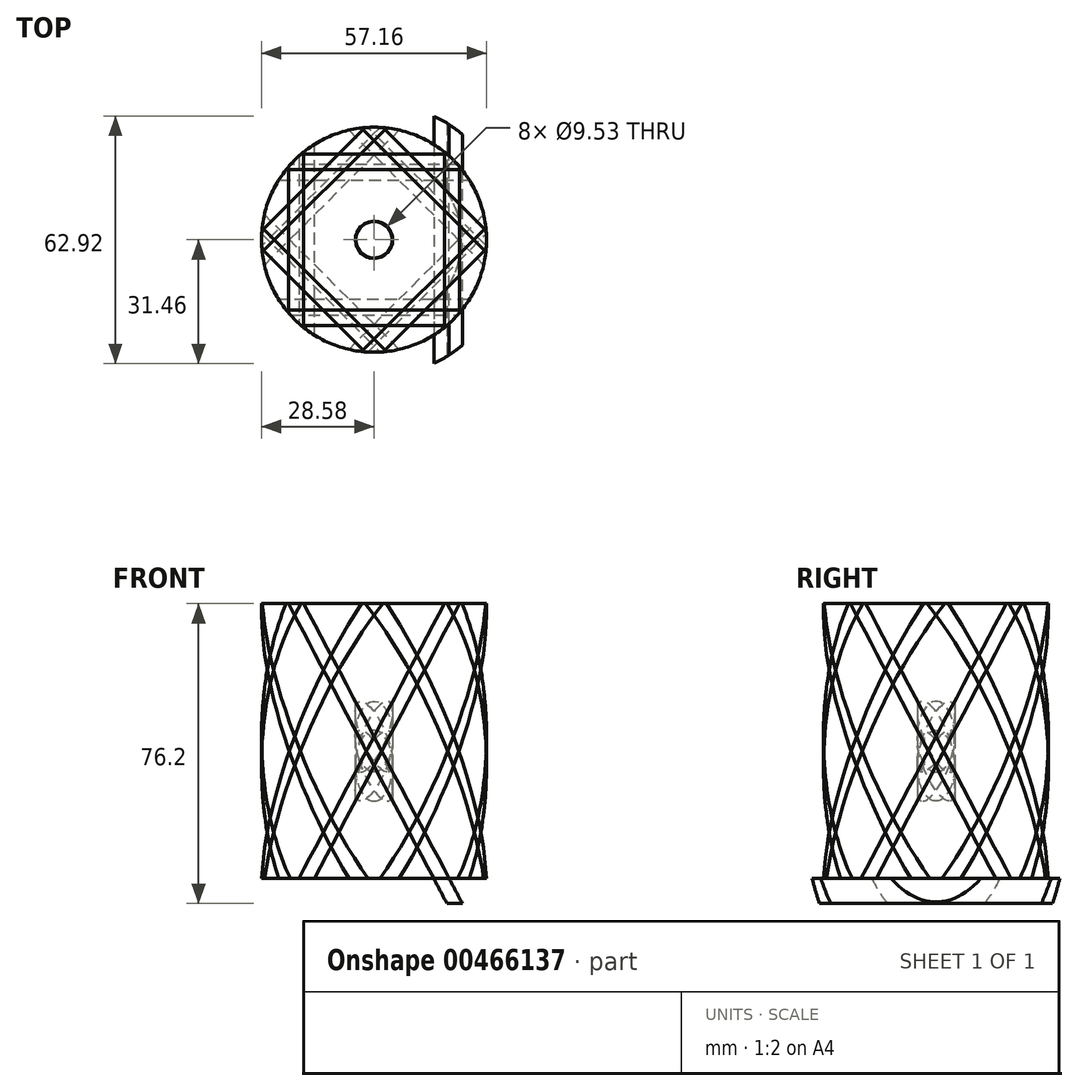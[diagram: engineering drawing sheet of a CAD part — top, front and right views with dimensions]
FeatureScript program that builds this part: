
annotation { "Feature Type Name" : "Feature", "Feature Type Description" : "" }
export const myFeature = defineFeature(function(context is Context, id is Id, definition is map)
    precondition{}
    {
        {
            var Q0;
            Q0=qCreatedBy(makeId("Top.planeOp"),FACE);
            var sketch = newSketch(context, id + "F0", { "sketchPlane" : qUnion([Q0])});
            skCircle(sketch, "E0", {"center": v(0, 0) * mm, "radius": 28.58 * mm});
            skCircle(sketch, "E1.0", {"center": v(0, 0) * mm, "radius": 22.22 * mm});
            skCircle(sketch, "E2", {"center": v(0, 0) * mm, "radius": 4.76 * mm});
            skCircle(sketch, "E3", {"center": v(0, 0) * mm, "radius": 34.93 * mm});
            skSolve(sketch);
        }
        {
            var Q0;
            Q0=qCreatedBy(makeId("Front.planeOp"),FACE);
            var sketch = newSketch(context, id + "F1", { "sketchPlane" : qUnion([Q0])});
            skLineSegment(sketch, "E4", {"start": v(-20.19, 74.24) * mm, "end": v(22.62, -6.7) * mm});
            skLineSegment(sketch, "E5", {"start": v(22.62, -6.7) * mm, "end": v(18.72, -6.7) * mm});
            skLineSegment(sketch, "E6", {"start": v(18.72, -6.7) * mm, "end": v(-24.1, 74.24) * mm});
            skLineSegment(sketch, "E7", {"start": v(-24.1, 74.24) * mm, "end": v(-20.19, 74.24) * mm});
            skLineSegment(sketch, "E8", {"start": v(0, 0) * mm, "end": v(0, 75.23) * mm, "construction": true});
            skSolve(sketch);
        }
        {
            var Q0;
            Q0=makeQuery(id+"F0.imprint","IMPRINT",FACE,{"disambiguationData":[TD([[makeQuery(id+"F0.imprint","IMPRINT",EDGE,{"derivedFrom":sQuery(id+"F0.wireOp",EDGE,"E0")}),-1.0]])]});
            var Q1;
            Q1=makeQuery(id+"F0.imprint","IMPRINT",FACE,{"disambiguationData":[TD([[makeQuery(id+"F0.imprint","IMPRINT",EDGE,{"derivedFrom":sQuery(id+"F0.wireOp",EDGE,"E0")}),1.0]])]});
            extrude(context, id + "F2", {"entities" : qUnion([Q0, Q1]), "oppositeDirection" : true, "depth" : 6.35 * mm});
        }
        {
            var Q0;
            Q0=makeQuery(id+"F0.imprint","IMPRINT",FACE,{"disambiguationData":[TD([[makeQuery(id+"F0.imprint","IMPRINT",EDGE,{"derivedFrom":sQuery(id+"F0.wireOp",EDGE,"E1.0")}),1.0]])]});
            var Q1;
            Q1=makeQuery(id+"F0.imprint","IMPRINT",FACE,{"disambiguationData":[TD([[makeQuery(id+"F0.imprint","IMPRINT",EDGE,{"derivedFrom":sQuery(id+"F0.wireOp",EDGE,"E0")}),1.0]])]});
            extrude(context, id + "F3", {"entities" : qUnion([Q0, Q1]), "depth" : 69.85 * mm});
        }
        {
            var Q0;
            Q0=qSketchRegion(id+"F1",true);
            extrude(context, id + "F4", {"entities" : qUnion([Q0]), "operationType" : NewBodyOperationType.INTERSECT, "depth" : 101.6 * mm, "symmetric" : true});
        }
        {
            var Q0;
            Q0=makeQuery(id+"F3.opExtrude","SWEPT_BODY",BODY,{"disambiguationData":[OSD([sQuery(id+"F0.wireOp",EDGE,"E0"),sQuery(id+"F0.wireOp",EDGE,"E2")])]});
            var Q1;
            Q1=sQuery(id+"F1.wireOp",EDGE,"E8");
            circularPattern(context, id + "F5", {"entities" : qUnion([Q0]), "axis" : qUnion([Q1]), "angle" : 360 * degree, "instanceCount" : 8, "equalSpace" : true});
        }
    });
